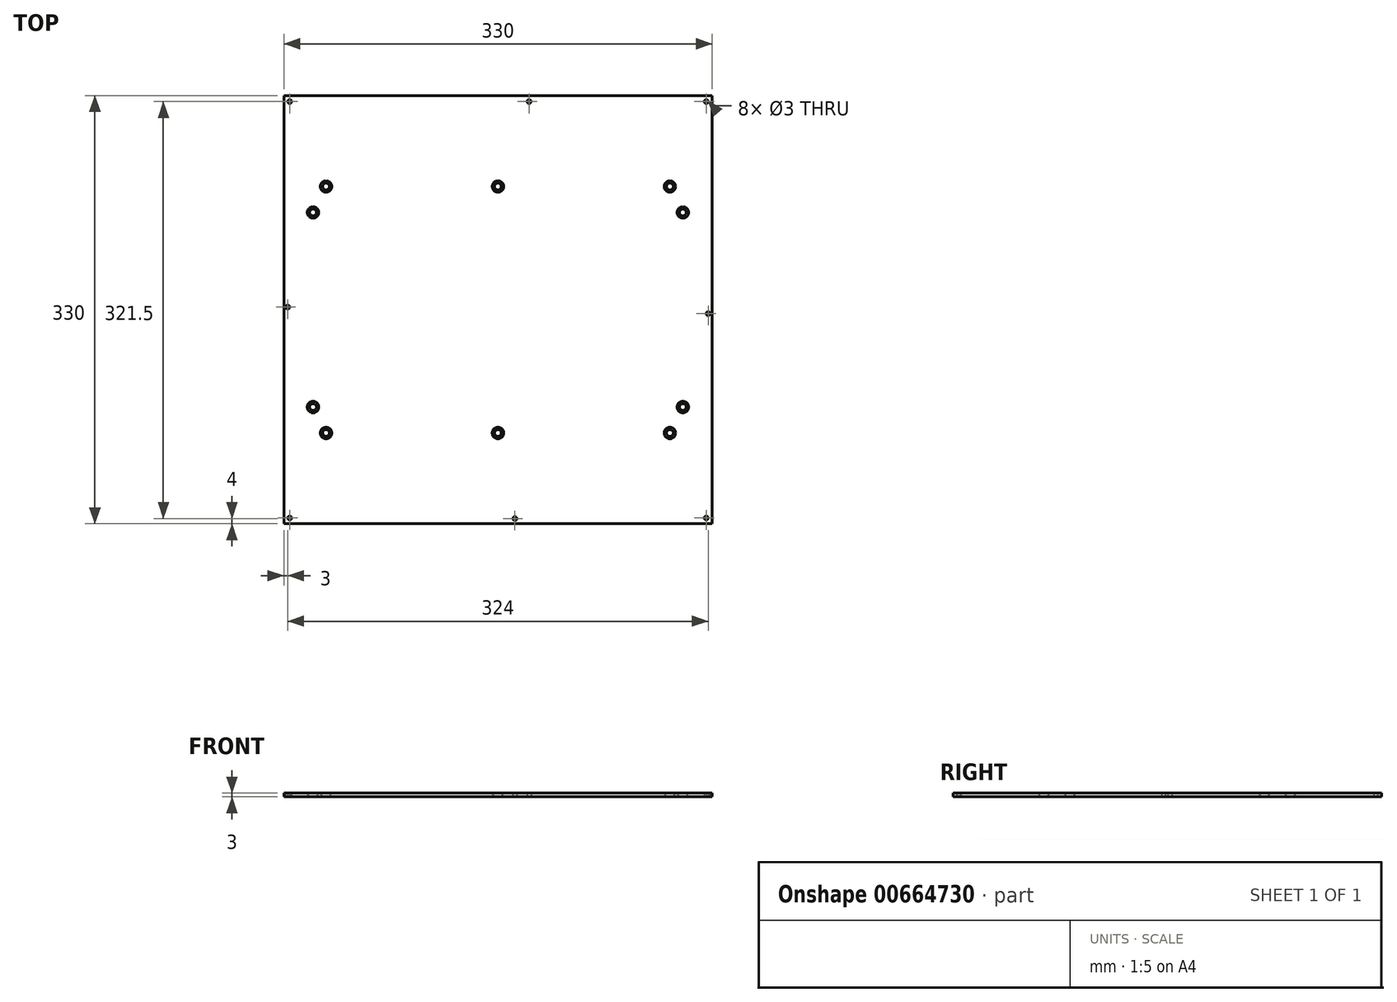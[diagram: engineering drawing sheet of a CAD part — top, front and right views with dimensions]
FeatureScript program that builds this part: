
annotation { "Feature Type Name" : "Feature", "Feature Type Description" : "" }
export const myFeature = defineFeature(function(context is Context, id is Id, definition is map)
    precondition{}
    {
        {
            var Q0;
            Q0=qCreatedBy(makeId("Top.planeOp"),FACE);
            var sketch = newSketch(context, id + "F0", { "sketchPlane" : qUnion([Q0])});
            skLineSegment(sketch, "E0.bottom", {"start": v(165, 165) * mm, "end": v(-165, 165) * mm});
            skLineSegment(sketch, "E0.top", {"start": v(165, -165) * mm, "end": v(-165, -165) * mm});
            skLineSegment(sketch, "E0.left", {"start": v(165, 165) * mm, "end": v(165, -165) * mm});
            skLineSegment(sketch, "E0.right", {"start": v(-165, 165) * mm, "end": v(-165, -165) * mm});
            skPoint(sketch, "E0.middle", {"position": v(0, 0) * mm});
            skCircle(sketch, "E1", {"center": v(160.5, 160.5) * mm, "radius": 1.5 * mm});
            skCircle(sketch, "E2", {"center": v(160.5, -160.5) * mm, "radius": 1.5 * mm});
            skCircle(sketch, "E3", {"center": v(-160.5, 160.5) * mm, "radius": 1.5 * mm});
            skCircle(sketch, "E4", {"center": v(-160.5, -160.5) * mm, "radius": 1.5 * mm});
            skCircle(sketch, "E5", {"center": v(24, 160.5) * mm, "radius": 1.5 * mm});
            skCircle(sketch, "E6", {"center": v(162, -3) * mm, "radius": 1.5 * mm});
            skCircle(sketch, "E7", {"center": v(-162, 2) * mm, "radius": 1.5 * mm});
            skCircle(sketch, "E8", {"center": v(13, -161) * mm, "radius": 1.5 * mm});
            skLineSegment(sketch, "E9", {"start": v(0, 165) * mm, "end": v(0, -165) * mm, "construction": true});
            skLineSegment(sketch, "E10", {"start": v(-165, 0) * mm, "end": v(165, 0) * mm, "construction": true});
            skLineSegment(sketch, "E11.0", {"start": v(152.5, 165) * mm, "end": v(152.5, -165) * mm, "construction": true});
            skLineSegment(sketch, "E12.0", {"start": v(-152.5, 165) * mm, "end": v(-152.5, -165) * mm, "construction": true});
            skLineSegment(sketch, "E13.0", {"start": v(-165, 105) * mm, "end": v(165, 105) * mm, "construction": true});
            skLineSegment(sketch, "E14.0", {"start": v(-165, -105) * mm, "end": v(165, -105) * mm, "construction": true});
            skLineSegment(sketch, "E15.0", {"start": v(-165, 95) * mm, "end": v(165, 95) * mm, "construction": true});
            skLineSegment(sketch, "E16.0", {"start": v(-165, -95) * mm, "end": v(165, -95) * mm, "construction": true});
            skLineSegment(sketch, "E17.0", {"start": v(-142.5, 165) * mm, "end": v(-142.5, -165) * mm, "construction": true});
            skLineSegment(sketch, "E18.0", {"start": v(142.5, 165) * mm, "end": v(142.5, -165) * mm, "construction": true});
            skLineSegment(sketch, "E19.0", {"start": v(-132.5, 165) * mm, "end": v(-132.5, -165) * mm, "construction": true});
            skLineSegment(sketch, "E20.0", {"start": v(132.5, 165) * mm, "end": v(132.5, -165) * mm, "construction": true});
            skLineSegment(sketch, "E21.0", {"start": v(-165, 75) * mm, "end": v(165, 75) * mm, "construction": true});
            skLineSegment(sketch, "E22.0", {"start": v(-165, -75) * mm, "end": v(165, -75) * mm, "construction": true});
            skCircle(sketch, "E23", {"center": v(-132.5, 95) * mm, "radius": 2.6 * mm});
            skCircle(sketch, "E24", {"center": v(132.5, 95) * mm, "radius": 2.6 * mm});
            skCircle(sketch, "E25", {"center": v(0, 95) * mm, "radius": 2.6 * mm});
            skCircle(sketch, "E26", {"center": v(132.5, -95) * mm, "radius": 2.6 * mm});
            skCircle(sketch, "E27", {"center": v(142.5, -75) * mm, "radius": 2.6 * mm});
            skCircle(sketch, "E28", {"center": v(142.5, 75) * mm, "radius": 2.6 * mm});
            skCircle(sketch, "E29", {"center": v(0, -95) * mm, "radius": 2.6 * mm});
            skCircle(sketch, "E30", {"center": v(-132.5, -95) * mm, "radius": 2.6 * mm});
            skCircle(sketch, "E31", {"center": v(-142.5, 75) * mm, "radius": 2.6 * mm});
            skCircle(sketch, "E32", {"center": v(-142.5, -75) * mm, "radius": 2.6 * mm});
            skSolve(sketch);
        }
        {
            var Q0;
            Q0=makeQuery(id+"F0.imprint","IMPRINT",FACE,{"disambiguationData":[TD([[makeQuery(id+"F0.imprint","IMPRINT",EDGE,{"derivedFrom":sQuery(id+"F0.wireOp",EDGE,"E0.bottom")}),1.0]])]});
            extrude(context, id + "F1", {"entities" : qUnion([Q0]), "depth" : 3 * mm, "offsetDistance" : 25 * mm});
        }
        {
            var Q0;
            Q0=makeQuery(id+"F1.opExtrude","CAP_EDGE",EDGE,{"disambiguationData":[OSD([sQuery(id+"F0.wireOp",EDGE,"E23")])],"isStart":false});
            chamfer(context, id + "F2", {"entities" : qUnion([Q0]), "chamferType" : ChamferType.OFFSET_ANGLE, "width" : 3 * mm, "oppositeDirection" : false, "angle" : 31.65 * degree, "tangentPropagation" : true});
        }
        {
            var Q0;
            Q0=makeQuery(id+"F1.opExtrude","CAP_EDGE",EDGE,{"disambiguationData":[OSD([sQuery(id+"F0.wireOp",EDGE,"E31")])],"isStart":false});
            var Q1;
            Q1=makeQuery(id+"F1.opExtrude","CAP_EDGE",EDGE,{"disambiguationData":[OSD([sQuery(id+"F0.wireOp",EDGE,"E25")])],"isStart":false});
            var Q2;
            Q2=makeQuery(id+"F1.opExtrude","CAP_EDGE",EDGE,{"disambiguationData":[OSD([sQuery(id+"F0.wireOp",EDGE,"E24")])],"isStart":false});
            var Q3;
            Q3=makeQuery(id+"F1.opExtrude","CAP_EDGE",EDGE,{"disambiguationData":[OSD([sQuery(id+"F0.wireOp",EDGE,"E28")])],"isStart":false});
            var Q4;
            Q4=makeQuery(id+"F1.opExtrude","CAP_EDGE",EDGE,{"disambiguationData":[OSD([sQuery(id+"F0.wireOp",EDGE,"E27")])],"isStart":false});
            var Q5;
            Q5=makeQuery(id+"F1.opExtrude","CAP_EDGE",EDGE,{"disambiguationData":[OSD([sQuery(id+"F0.wireOp",EDGE,"E26")])],"isStart":false});
            var Q6;
            Q6=makeQuery(id+"F1.opExtrude","CAP_EDGE",EDGE,{"disambiguationData":[OSD([sQuery(id+"F0.wireOp",EDGE,"E29")])],"isStart":false});
            var Q7;
            Q7=makeQuery(id+"F1.opExtrude","CAP_EDGE",EDGE,{"disambiguationData":[OSD([sQuery(id+"F0.wireOp",EDGE,"E30")])],"isStart":false});
            var Q8;
            Q8=makeQuery(id+"F1.opExtrude","CAP_EDGE",EDGE,{"disambiguationData":[OSD([sQuery(id+"F0.wireOp",EDGE,"E32")])],"isStart":false});
            chamfer(context, id + "F3", {"entities" : qUnion([Q0, Q1, Q2, Q3, Q4, Q5, Q6, Q7, Q8]), "chamferType" : ChamferType.OFFSET_ANGLE, "width" : 3 * mm, "oppositeDirection" : false, "angle" : 31.65 * degree, "tangentPropagation" : true});
        }
    });
